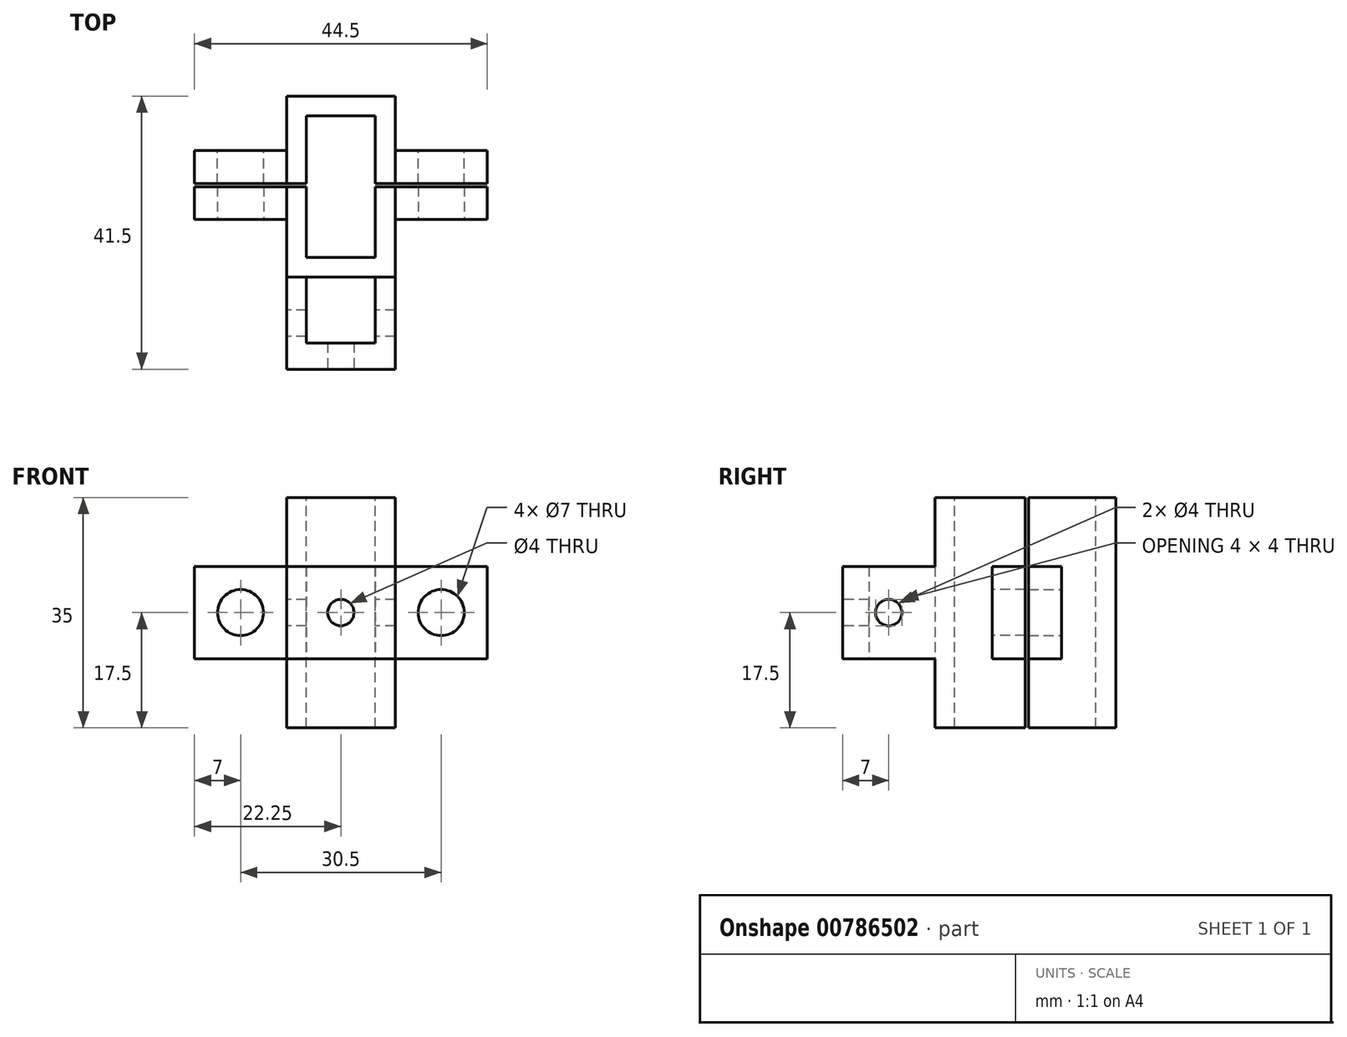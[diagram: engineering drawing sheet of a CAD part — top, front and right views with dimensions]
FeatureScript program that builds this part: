
annotation { "Feature Type Name" : "Feature", "Feature Type Description" : "" }
export const myFeature = defineFeature(function(context is Context, id is Id, definition is map)
    precondition{}
    {
        {
            var Q0;
            Q0=qCreatedBy(makeId("Top.planeOp"),FACE);
            var sketch = newSketch(context, id + "F0", { "sketchPlane" : qUnion([Q0])});
            skLineSegment(sketch, "E0.bottom", {"start": v(0, 0) * mm, "end": v(-16.5, 0) * mm});
            skLineSegment(sketch, "E0.top", {"start": v(0, -27.5) * mm, "end": v(-16.5, -27.5) * mm});
            skLineSegment(sketch, "E0.left", {"start": v(0, 0) * mm, "end": v(0, -27.5) * mm});
            skLineSegment(sketch, "E0.right", {"start": v(-16.5, 0) * mm, "end": v(-16.5, -27.5) * mm});
            skSolve(sketch);
        }
        {
            var Q0;
            Q0 = qSketchRegion(id + "F0", true);
            extrude(context, id + "F1", {"entities" : qUnion([Q0]), "depth" : 35 * mm, "offsetDistance" : 25 * mm});
        }
        {
            var Q0;
            Q0=makeQuery(id+"F1.opExtrude","CAP_FACE",FACE,{"disambiguationData":[OSD([sQuery(id+"F0.wireOp",EDGE,"E0.bottom"),sQuery(id+"F0.wireOp",EDGE,"E0.top"),sQuery(id+"F0.wireOp",EDGE,"E0.left"),sQuery(id+"F0.wireOp",EDGE,"E0.right")])],"isStart":false});
            var sketch = newSketch(context, id + "F2", { "sketchPlane" : qUnion([Q0])});
            skLineSegment(sketch, "E1.bottom", {"start": v(-3, -3) * mm, "end": v(-13.5, -3) * mm});
            skLineSegment(sketch, "E1.top", {"start": v(-3, -24.5) * mm, "end": v(-13.5, -24.5) * mm});
            skLineSegment(sketch, "E1.left", {"start": v(-3, -3) * mm, "end": v(-3, -24.5) * mm});
            skLineSegment(sketch, "E1.right", {"start": v(-13.5, -3) * mm, "end": v(-13.5, -24.5) * mm});
            skSolve(sketch);
        }
        {
            var Q0;
            Q0 = qSketchRegion(id + "F2", true);
            extrude(context, id + "F3", {"entities" : qUnion([Q0]), "operationType" : NewBodyOperationType.REMOVE, "oppositeDirection" : true, "depth" : 35 * mm, "offsetDistance" : 25 * mm});
        }
        {
            var Q0;
            Q0=makeQuery(id+"F1.opExtrude","CAP_FACE",FACE,{"disambiguationData":[OSD([sQuery(id+"F0.wireOp",EDGE,"E0.bottom"),sQuery(id+"F0.wireOp",EDGE,"E0.top"),sQuery(id+"F0.wireOp",EDGE,"E0.left"),sQuery(id+"F0.wireOp",EDGE,"E0.right")])],"isStart":false});
            var sketch = newSketch(context, id + "F4", { "sketchPlane" : qUnion([Q0])});
            skLineSegment(sketch, "E2.bottom", {"start": v(0, -13.75) * mm, "end": v(-3, -13.75) * mm});
            skLineSegment(sketch, "E2.top", {"start": v(0, -13.25) * mm, "end": v(-3, -13.25) * mm});
            skLineSegment(sketch, "E2.left", {"start": v(0, -13.75) * mm, "end": v(0, -13.25) * mm});
            skLineSegment(sketch, "E2.right", {"start": v(-3, -13.75) * mm, "end": v(-3, -13.25) * mm});
            skLineSegment(sketch, "E3.bottom", {"start": v(-13.5, -13.75) * mm, "end": v(-16.5, -13.75) * mm});
            skLineSegment(sketch, "E3.top", {"start": v(-13.5, -13.25) * mm, "end": v(-16.5, -13.25) * mm});
            skLineSegment(sketch, "E3.left", {"start": v(-13.5, -13.75) * mm, "end": v(-13.5, -13.25) * mm});
            skLineSegment(sketch, "E3.right", {"start": v(-16.5, -13.75) * mm, "end": v(-16.5, -13.25) * mm});
            skSolve(sketch);
        }
        {
            var Q0;
            Q0 = qSketchRegion(id + "F4", true);
            extrude(context, id + "F5", {"entities" : qUnion([Q0]), "operationType" : NewBodyOperationType.REMOVE, "oppositeDirection" : true, "depth" : 35 * mm, "offsetDistance" : 25 * mm});
        }
        {
            var Q0;
            {var subQ0=sQuery(id+"F0.wireOp",EDGE,"E0.right");var subQ2=sQuery(id+"F0.wireOp",EDGE,"E0.top");Q0=makeQuery(id+"F5.boolean.opBoolean","SPLIT",FACE,{"disambiguationData":[TD([makeQuery(id+"F1.opExtrude","SWEPT_FACE",FACE,{"disambiguationData":[OSD([subQ2])]})])],"derivedFrom":makeQuery(id+"F1.opExtrude","SWEPT_FACE",FACE,{"disambiguationData":[OSD([subQ0])]})});}
            var sketch = newSketch(context, id + "F6", { "sketchPlane" : qUnion([Q0])});
            skLineSegment(sketch, "E4.bottom", {"start": v(13.75, 24.5) * mm, "end": v(18.75, 24.5) * mm});
            skLineSegment(sketch, "E4.top", {"start": v(13.75, 10.5) * mm, "end": v(18.75, 10.5) * mm});
            skLineSegment(sketch, "E4.left", {"start": v(13.75, 24.5) * mm, "end": v(13.75, 10.5) * mm});
            skLineSegment(sketch, "E4.right", {"start": v(18.75, 24.5) * mm, "end": v(18.75, 10.5) * mm});
            skSolve(sketch);
        }
        {
            var Q0;
            Q0 = qSketchRegion(id + "F6", true);
            extrude(context, id + "F7", {"entities" : qUnion([Q0]), "operationType" : NewBodyOperationType.ADD, "depth" : 14 * mm, "offsetDistance" : 25 * mm});
        }
        {
            var Q0;
            Q0=makeQuery(id+"F7.opExtrude","SWEPT_FACE",FACE,{"disambiguationData":[OSD([sQuery(id+"F6.wireOp",EDGE,"E4.right")])]});
            var sketch = newSketch(context, id + "F8", { "sketchPlane" : qUnion([Q0])});
            skCircle(sketch, "E5", {"center": v(-23.5, 17.5) * mm, "radius": 3.5 * mm});
            skPoint(sketch, "E5.centerSnap0", {"position": v(-30.5, 17.5) * mm});
            skPoint(sketch, "E5.centerSnap1", {"position": v(-23.5, 24.5) * mm});
            skSolve(sketch);
        }
        {
            var Q0;
            Q0 = qSketchRegion(id + "F8", true);
            extrude(context, id + "F9", {"entities" : qUnion([Q0]), "operationType" : NewBodyOperationType.REMOVE, "oppositeDirection" : true, "depth" : 5 * mm, "offsetDistance" : 25 * mm});
        }
        {
            var Q0;
            {var subQ0=sQuery(id+"F0.wireOp",EDGE,"E0.right");var subQ2=sQuery(id+"F0.wireOp",EDGE,"E0.top");Q0=makeQuery(id+"F5.boolean.opBoolean","SPLIT",FACE,{"disambiguationData":[TD([makeQuery(id+"F1.opExtrude","SWEPT_FACE",FACE,{"disambiguationData":[OSD([subQ2])]})])],"derivedFrom":makeQuery(id+"F1.opExtrude","SWEPT_FACE",FACE,{"disambiguationData":[OSD([subQ0])]})});}
            cPlane(context, id + "F10", {"entities" : qUnion([Q0]), "cplaneType" : CPlaneType.OFFSET, "offset" : 8.25 * mm, "oppositeDirection" : true, "width" : 150 * mm, "height" : 150 * mm});
        }
        {
            var Q0;
            Q0=makeQuery(id+"F5.boolean.opBoolean","SPLIT",BODY,{"disambiguationData":[OD(1.0)],"derivedFrom":makeQuery(id+"F1.opExtrude","SWEPT_BODY",BODY,{"disambiguationData":[OSD([sQuery(id+"F0.wireOp",EDGE,"E0.bottom"),sQuery(id+"F0.wireOp",EDGE,"E0.top"),sQuery(id+"F0.wireOp",EDGE,"E0.left"),sQuery(id+"F0.wireOp",EDGE,"E0.right")])]})});
            var Q1;
            Q1=qCreatedBy(id+"F10.planeOp",FACE);
            mirror(context, id + "F11", {"operationType" : NewBodyOperationType.ADD, "entities" : qUnion([Q0]), "mirrorPlane" : qUnion([Q1])});
        }
        {
            var Q0;
            {var subQ0=sQuery(id+"F0.wireOp",EDGE,"E0.bottom");var subQ1=sQuery(id+"F0.wireOp",EDGE,"E0.right");Q0=makeQuery(id+"F5.boolean.opBoolean","SPLIT",FACE,{"disambiguationData":[TD([makeQuery(id+"F1.opExtrude","SWEPT_FACE",FACE,{"disambiguationData":[OSD([subQ0])]})])],"derivedFrom":makeQuery(id+"F1.opExtrude","SWEPT_FACE",FACE,{"disambiguationData":[OSD([subQ1])]})});}
            var sketch = newSketch(context, id + "F12", { "sketchPlane" : qUnion([Q0])});
            skLineSegment(sketch, "E6.bottom", {"start": v(13.25, 24.5) * mm, "end": v(8.25, 24.5) * mm});
            skLineSegment(sketch, "E6.top", {"start": v(13.25, 10.5) * mm, "end": v(8.25, 10.5) * mm});
            skLineSegment(sketch, "E6.left", {"start": v(13.25, 24.5) * mm, "end": v(13.25, 10.5) * mm});
            skLineSegment(sketch, "E6.right", {"start": v(8.25, 24.5) * mm, "end": v(8.25, 10.5) * mm});
            skSolve(sketch);
        }
        {
            var Q0;
            Q0 = qSketchRegion(id + "F12", true);
            extrude(context, id + "F13", {"entities" : qUnion([Q0]), "operationType" : NewBodyOperationType.ADD, "depth" : 14 * mm, "offsetDistance" : 25 * mm});
        }
        {
            var Q0;
            Q0=makeQuery(id+"F13.opExtrude","SWEPT_FACE",FACE,{"disambiguationData":[OSD([sQuery(id+"F12.wireOp",EDGE,"E6.right")])]});
            var sketch = newSketch(context, id + "F14", { "sketchPlane" : qUnion([Q0])});
            skCircle(sketch, "E7", {"center": v(23.5, 17.5) * mm, "radius": 3.5 * mm});
            skPoint(sketch, "E7.centerSnap0", {"position": v(16.5, 17.5) * mm});
            skPoint(sketch, "E7.centerSnap1", {"position": v(23.5, 24.5) * mm});
            skSolve(sketch);
        }
        {
            var Q0;
            Q0 = qSketchRegion(id + "F14", true);
            extrude(context, id + "F15", {"entities" : qUnion([Q0]), "operationType" : NewBodyOperationType.REMOVE, "oppositeDirection" : true, "depth" : 255 * mm, "offsetDistance" : 25 * mm});
        }
        {
            var Q0;
            Q0=makeQuery(id+"F5.boolean.opBoolean","SPLIT",BODY,{"disambiguationData":[OD(0.0)],"derivedFrom":makeQuery(id+"F1.opExtrude","SWEPT_BODY",BODY,{"disambiguationData":[OSD([sQuery(id+"F0.wireOp",EDGE,"E0.bottom"),sQuery(id+"F0.wireOp",EDGE,"E0.top"),sQuery(id+"F0.wireOp",EDGE,"E0.left"),sQuery(id+"F0.wireOp",EDGE,"E0.right")])]})});
            var Q1;
            Q1=qCreatedBy(id+"F10.planeOp",FACE);
            mirror(context, id + "F16", {"operationType" : NewBodyOperationType.ADD, "entities" : qUnion([Q0]), "mirrorPlane" : qUnion([Q1])});
        }
        {
            var Q0;
            Q0=makeQuery(id+"F1.opExtrude","SWEPT_FACE",FACE,{"disambiguationData":[OSD([sQuery(id+"F0.wireOp",EDGE,"E0.top")])]});
            var sketch = newSketch(context, id + "F17", { "sketchPlane" : qUnion([Q0])});
            skLineSegment(sketch, "E8.bottom", {"start": v(-16.5, 24.5) * mm, "end": v(-13.5, 24.5) * mm});
            skLineSegment(sketch, "E8.top", {"start": v(-16.5, 10.5) * mm, "end": v(-13.5, 10.5) * mm});
            skLineSegment(sketch, "E8.left", {"start": v(-16.5, 24.5) * mm, "end": v(-16.5, 10.5) * mm});
            skLineSegment(sketch, "E8.right", {"start": v(-13.5, 24.5) * mm, "end": v(-13.5, 10.5) * mm});
            skLineSegment(sketch, "E9.MirrorCS", {"start": v(-3, 24.5) * mm, "end": v(-3, 10.5) * mm});
            skLineSegment(sketch, "E10.MirrorCS", {"start": v(0, 24.5) * mm, "end": v(-3, 24.5) * mm});
            skLineSegment(sketch, "E11.MirrorCS", {"start": v(0, 10.5) * mm, "end": v(-3, 10.5) * mm});
            skLineSegment(sketch, "E12.MirrorCS", {"start": v(0, 24.5) * mm, "end": v(0, 10.5) * mm});
            skSolve(sketch);
        }
        {
            var Q0;
            Q0 = qSketchRegion(id + "F17", true);
            extrude(context, id + "F18", {"entities" : qUnion([Q0]), "operationType" : NewBodyOperationType.ADD, "depth" : 10 * mm, "offsetDistance" : 25 * mm});
        }
        {
            var Q0;
            Q0=makeQuery(id+"F18.opExtrude","CAP_FACE",FACE,{"disambiguationData":[OSD([sQuery(id+"F17.wireOp",EDGE,"E8.bottom"),sQuery(id+"F17.wireOp",EDGE,"E8.top"),sQuery(id+"F17.wireOp",EDGE,"E8.left"),sQuery(id+"F17.wireOp",EDGE,"E8.right")])],"isStart":false});
            var sketch = newSketch(context, id + "F19", { "sketchPlane" : qUnion([Q0])});
            skLineSegment(sketch, "E13.bottom", {"start": v(-16.5, 24.5) * mm, "end": v(0, 24.5) * mm});
            skLineSegment(sketch, "E13.top", {"start": v(-16.5, 10.5) * mm, "end": v(0, 10.5) * mm});
            skLineSegment(sketch, "E13.left", {"start": v(-16.5, 24.5) * mm, "end": v(-16.5, 10.5) * mm});
            skLineSegment(sketch, "E13.right", {"start": v(0, 24.5) * mm, "end": v(0, 10.5) * mm});
            skSolve(sketch);
        }
        {
            var Q0;
            Q0 = qSketchRegion(id + "F19", true);
            extrude(context, id + "F20", {"entities" : qUnion([Q0]), "operationType" : NewBodyOperationType.ADD, "depth" : 4 * mm, "offsetDistance" : 25 * mm});
        }
        {
            var Q0;
            Q0=makeQuery(id+"F20.opExtrude","CAP_FACE",FACE,{"disambiguationData":[OSD([sQuery(id+"F19.wireOp",EDGE,"E13.bottom"),sQuery(id+"F19.wireOp",EDGE,"E13.top"),sQuery(id+"F19.wireOp",EDGE,"E13.left"),sQuery(id+"F19.wireOp",EDGE,"E13.right")])],"isStart":false});
            var sketch = newSketch(context, id + "F21", { "sketchPlane" : qUnion([Q0])});
            skCircle(sketch, "E14", {"center": v(-8.25, 17.5) * mm, "radius": 2 * mm});
            skPoint(sketch, "E14.centerSnap0", {"position": v(-16.5, 17.5) * mm});
            skPoint(sketch, "E14.centerSnap1", {"position": v(-8.25, 24.5) * mm});
            skSolve(sketch);
        }
        {
            var Q0;
            Q0 = qSketchRegion(id + "F21", true);
            extrude(context, id + "F22", {"entities" : qUnion([Q0]), "operationType" : NewBodyOperationType.REMOVE, "oppositeDirection" : true, "depth" : 4 * mm, "offsetDistance" : 25 * mm});
        }
        {
            var Q0;
            {var subQ0=sQuery(id+"F0.wireOp",EDGE,"E0.right");var subQ2=sQuery(id+"F0.wireOp",EDGE,"E0.top");Q0=makeQuery(id+"F20.boolean.opBoolean","MERGE",FACE,{"derivedFrom":[makeQuery(id+"F18.boolean.opBoolean","MERGE",FACE,{"derivedFrom":[makeQuery(id+"F5.boolean.opBoolean","SPLIT",FACE,{"disambiguationData":[TD([makeQuery(id+"F1.opExtrude","SWEPT_FACE",FACE,{"disambiguationData":[OSD([subQ2])]})])],"derivedFrom":makeQuery(id+"F1.opExtrude","SWEPT_FACE",FACE,{"disambiguationData":[OSD([subQ0])]})}),makeQuery(id+"F18.opExtrude","SWEPT_FACE",FACE,{"disambiguationData":[OSD([sQuery(id+"F17.wireOp",EDGE,"E8.left")])]})]}),makeQuery(id+"F20.opExtrude","SWEPT_FACE",FACE,{"disambiguationData":[OSD([sQuery(id+"F19.wireOp",EDGE,"E13.left")])]})]});}
            var sketch = newSketch(context, id + "F23", { "sketchPlane" : qUnion([Q0])});
            skCircle(sketch, "E15", {"center": v(34.5, 17.5) * mm, "radius": 2 * mm});
            skPoint(sketch, "E15.centerSnap0", {"position": v(41.5, 17.5) * mm});
            skPoint(sketch, "E15.centerSnap1", {"position": v(34.5, 24.5) * mm});
            skSolve(sketch);
        }
        {
            var Q0;
            Q0 = qSketchRegion(id + "F23", true);
            extrude(context, id + "F24", {"entities" : qUnion([Q0]), "operationType" : NewBodyOperationType.REMOVE, "oppositeDirection" : true, "depth" : 16.5 * mm, "offsetDistance" : 25 * mm});
        }
    });
